# Revit family: Paladex_Pipe_System-Giunto_Bicchiere (13)
name_source: partatom
category: Accessori per tubazioni
units: mm (PartAtom-declared; Revit-internal decimal feet)

## family parameters
Basato su piano di lavoro = Sì
Condiviso = No
Numero OmniClass = 23.45.00.00
Quota connettore circolare = Usa diametro
Sempre verticale = No
Taglio con vuoti quando caricato = No
Tipo di parte = Normale
Titolo OmniClass = Sanitary, Laundry, and Cleaning Equipment

## types (25) — shared parameters
Dati = Paladex_Pipe_System (12)
Descrizione = PALADEX Tubo Spiralato Composito in Polietilene e Acciaio Zincato
ENG = No
Immagine tipo = <Nessuno>
Modello = Giunto Bicchiere
Produttore = Paladex
URL = www.paladeri.it
URL Manufacturer = www.paladeri.it
zero-valued in all types: Prospetto di default

## per-type parameters (varying)
| type | DN | URL "Lib bim" | h |
| 24 Ø2500 | 2500 mm | www.paladeri.it | 50 mm  [stored 0.164042 ft] |
| 23 Ø2400 | 2400 mm |  | 50 mm  [stored 0.164042 ft] |
| 22 Ø2300 | 2300 mm |  | 50 mm  [stored 0.164042 ft] |
| 21 Ø2200 | 2200 mm |  | 50 mm  [stored 0.164042 ft] |
| 20 Ø2100 | 2100 mm |  | 50 mm  [stored 0.164042 ft] |
| 19 Ø2000 | 2000 mm |  | 50 mm  [stored 0.164042 ft] |
| 18 Ø1900 | 1900 mm |  | 50 mm  [stored 0.164042 ft] |
| 17 Ø1800 | 1800 mm |  | 50 mm  [stored 0.164042 ft] |
| 16 Ø1640 | 1640 mm |  | 80 mm |
| 15 Ø1527 | 1527 mm |  | 57 mm |
| 14 Ø1500 | 1500 mm |  | 70 mm |
| 13 Ø1400 | 1400 mm |  | 64 mm |
| 12 Ø1300 | 1300 mm |  | 50 mm  [stored 0.164042 ft] |
| 11 Ø1200 | 1200 mm |  | 50 mm  [stored 0.164042 ft] |
| 10 Ø1100 | 1100 mm |  | 50 mm  [stored 0.164042 ft] |
| 09 Ø1000 | 1000 mm |  | 50 mm  [stored 0.164042 ft] |
| 08 Ø900 | 900 mm |  | 50 mm  [stored 0.164042 ft] |
| 07 Ø800 | 800 mm |  | 40 mm |
| 06 Ø750 | 750 mm |  | 40 mm |
| 05 Ø700 | 700 mm |  | 40 mm |
| 04 Ø600 | 600 mm |  | 28 mm |
| 03 Ø500 | 500 mm |  | 25 mm  [stored 0.082021 ft] |
| 02 Ø450 | 450 mm |  | 25 mm  [stored 0.082021 ft] |
| 01 Ø400 | 400 mm |  | 25 mm  [stored 0.082021 ft] |
| z ØSit | 400 mm |  | 25 mm  [stored 0.082021 ft] |

note: [stored X ft] marks values corroborated as IEEE doubles in the binary element streams (Revit-internal decimal feet)
